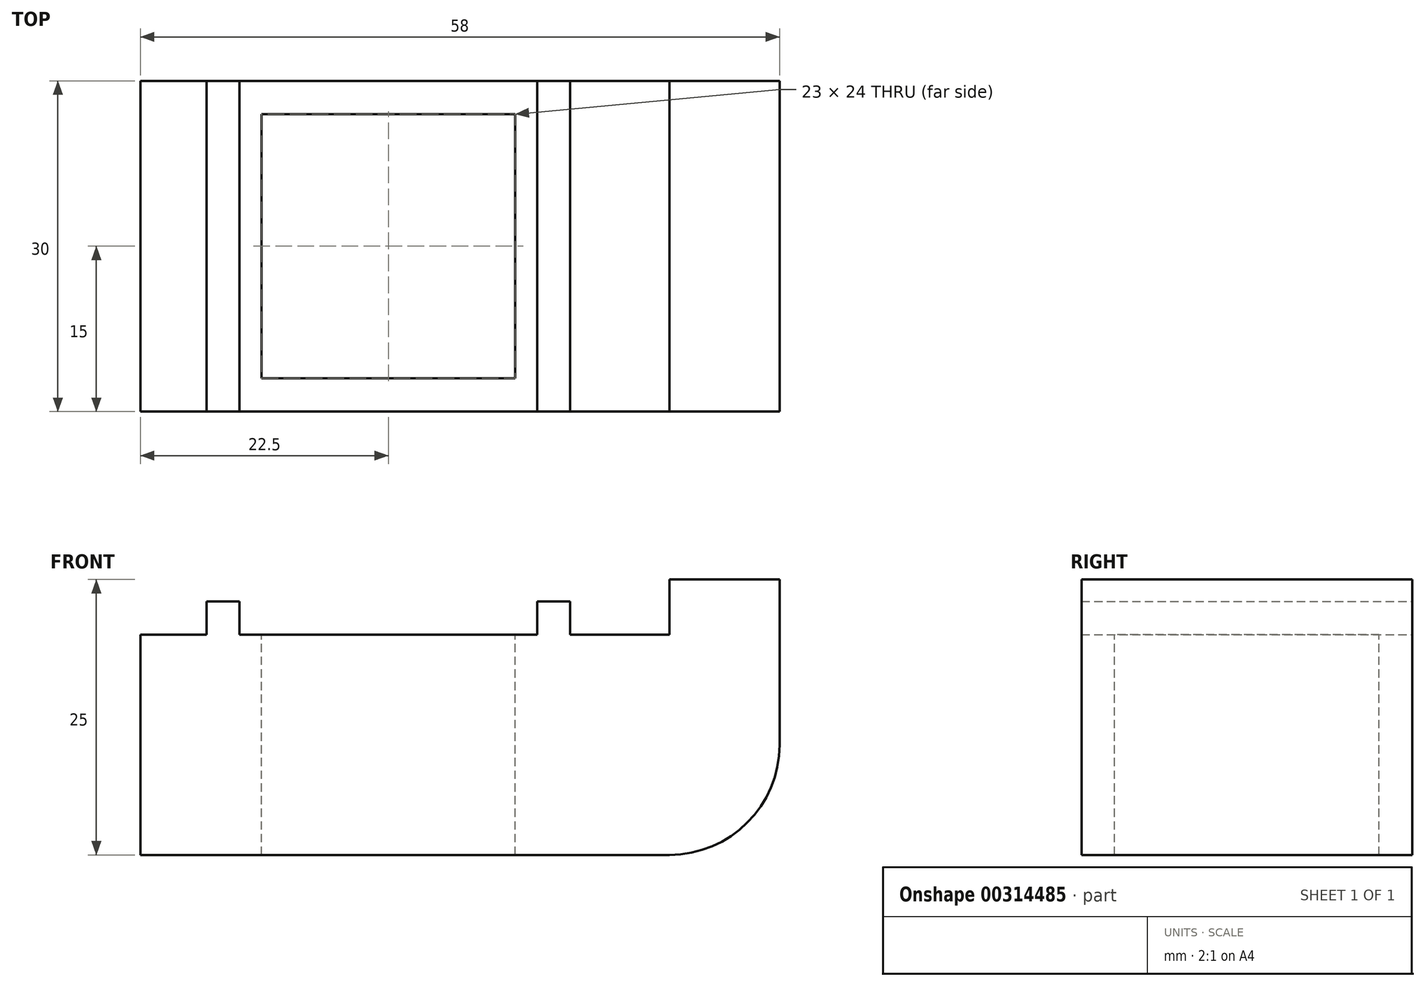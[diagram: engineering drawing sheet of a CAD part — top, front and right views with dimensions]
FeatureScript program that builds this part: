
annotation { "Feature Type Name" : "Feature", "Feature Type Description" : "" }
export const myFeature = defineFeature(function(context is Context, id is Id, definition is map)
    precondition{}
    {
        {
            var Q0;
            Q0=qCreatedBy(makeId("Front.planeOp"),FACE);
            var sketch = newSketch(context, id + "F0", { "sketchPlane" : qUnion([Q0])});
            skLineSegment(sketch, "E0", {"start": v(0, 0) * mm, "end": v(0, 20) * mm});
            skLineSegment(sketch, "E1", {"start": v(0, 20) * mm, "end": v(6, 20) * mm});
            skLineSegment(sketch, "E2", {"start": v(6, 20) * mm, "end": v(6, 23) * mm});
            skLineSegment(sketch, "E3", {"start": v(6, 23) * mm, "end": v(9, 23) * mm});
            skLineSegment(sketch, "E4", {"start": v(9, 23) * mm, "end": v(9, 20) * mm});
            skLineSegment(sketch, "E5", {"start": v(9, 20) * mm, "end": v(36, 20) * mm});
            skLineSegment(sketch, "E6", {"start": v(36, 20) * mm, "end": v(36, 23) * mm});
            skLineSegment(sketch, "E7", {"start": v(36, 23) * mm, "end": v(39, 23) * mm});
            skLineSegment(sketch, "E8", {"start": v(39, 23) * mm, "end": v(39, 20) * mm});
            skLineSegment(sketch, "E9", {"start": v(39, 20) * mm, "end": v(48, 20) * mm});
            skLineSegment(sketch, "E10", {"start": v(48, 20) * mm, "end": v(48, 25) * mm});
            skLineSegment(sketch, "E11", {"start": v(48, 25) * mm, "end": v(58, 25) * mm});
            skLineSegment(sketch, "E12", {"start": v(58, 25) * mm, "end": v(58, 10) * mm});
            skLineSegment(sketch, "E13", {"start": v(48, 0) * mm, "end": v(0, 0) * mm});
            skPoint(sketch, "E14.visualSharp", {"position": v(58, 0) * mm});
            skArc(sketch, "E14.filletArc", {"start": v(48, 0) * mm, "mid": v(55.07, 2.93) * mm, "end": v(58, 10) * mm});
            skSolve(sketch);
        }
        {
            var Q0;
            Q0=makeQuery(id+"F0.imprint","IMPRINT",FACE,{"disambiguationData":[TD([[makeQuery(id+"F0.imprint","IMPRINT",EDGE,{"derivedFrom":sQuery(id+"F0.wireOp",EDGE,"E0")}),-1.0]])]});
            extrude(context, id + "F1", {"entities" : qUnion([Q0]), "depth" : 30 * mm});
        }
        {
            var Q0;
            Q0=makeQuery(id+"F1.opExtrude","SWEPT_FACE",FACE,{"disambiguationData":[OSD([sQuery(id+"F0.wireOp",EDGE,"E5")])]});
            var sketch = newSketch(context, id + "F2", { "sketchPlane" : qUnion([Q0])});
            skLineSegment(sketch, "E15.bottom", {"start": v(11, -3) * mm, "end": v(34, -3) * mm});
            skLineSegment(sketch, "E15.top", {"start": v(11, -27) * mm, "end": v(34, -27) * mm});
            skLineSegment(sketch, "E15.left", {"start": v(11, -3) * mm, "end": v(11, -27) * mm});
            skLineSegment(sketch, "E15.right", {"start": v(34, -3) * mm, "end": v(34, -27) * mm});
            skSolve(sketch);
        }
        {
            var Q0;
            Q0=makeQuery(id+"F2.imprint","IMPRINT",FACE,{"disambiguationData":[TD([[makeQuery(id+"F2.imprint","IMPRINT",EDGE,{"derivedFrom":sQuery(id+"F2.wireOp",EDGE,"E15.bottom")}),-1.0]])]});
            extrude(context, id + "F3", {"entities" : qUnion([Q0]), "operationType" : NewBodyOperationType.REMOVE, "endBound" : BoundingType.THROUGH_ALL, "oppositeDirection" : true, "depth" : 25 * mm});
        }
    });
